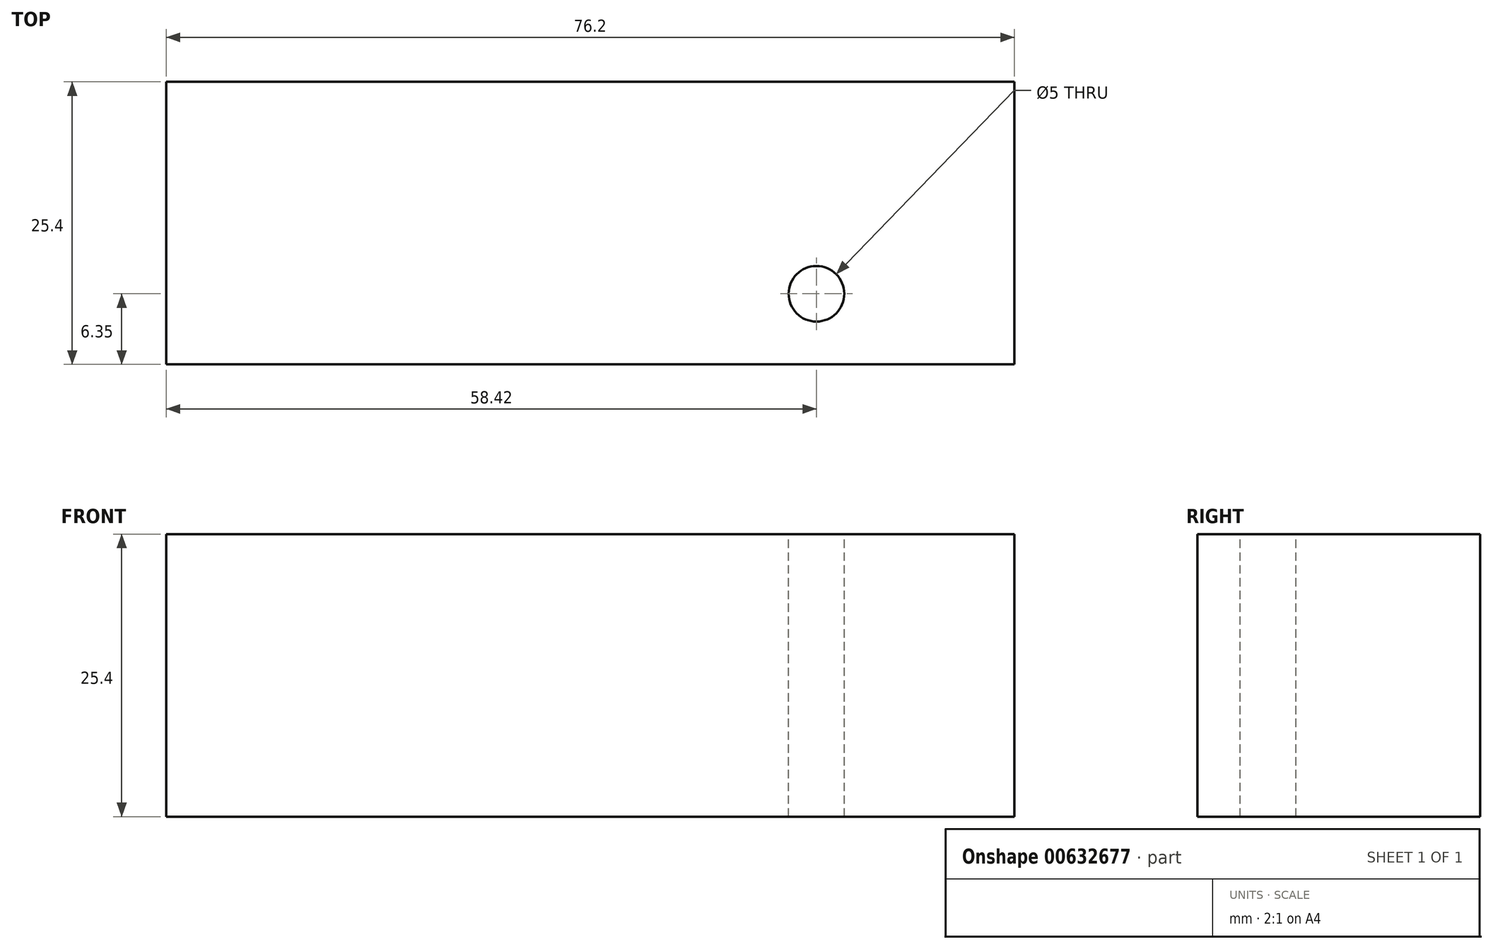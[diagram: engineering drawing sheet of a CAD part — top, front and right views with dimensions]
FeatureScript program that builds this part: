
annotation { "Feature Type Name" : "Feature", "Feature Type Description" : "" }
export const myFeature = defineFeature(function(context is Context, id is Id, definition is map)
    precondition{}
    {
        {
            var Q0;
            Q0=qCreatedBy(makeId("Front.planeOp"),FACE);
            var sketch = newSketch(context, id + "F0", { "sketchPlane" : qUnion([Q0])});
            skLineSegment(sketch, "E0.bottom", {"start": v(38.1, -12.7) * mm, "end": v(-38.1, -12.7) * mm});
            skLineSegment(sketch, "E0.top", {"start": v(38.1, 12.7) * mm, "end": v(-38.1, 12.7) * mm});
            skLineSegment(sketch, "E0.left", {"start": v(38.1, -12.7) * mm, "end": v(38.1, 12.7) * mm});
            skLineSegment(sketch, "E0.right", {"start": v(-38.1, -12.7) * mm, "end": v(-38.1, 12.7) * mm});
            skPoint(sketch, "E0.middle", {"position": v(0, 0) * mm});
            skSolve(sketch);
        }
        {
            var Q0;
            Q0 = qSketchRegion(id + "F0", true);
            extrude(context, id + "F1", {"entities" : qUnion([Q0]), "depth" : 25.4 * mm, "offsetDistance" : 25.4 * mm});
        }
        {
            var Q0;
            Q0=makeQuery(id+"F1.opExtrude","SWEPT_FACE",FACE,{"disambiguationData":[OSD([sQuery(id+"F0.wireOp",EDGE,"E0.top")])]});
            var sketch = newSketch(context, id + "F2", { "sketchPlane" : qUnion([Q0])});
            skPoint(sketch, "E1", {"position": v(20.32, -19.05) * mm});
            skSolve(sketch);
        }
        {
            var Q0;
            Q0=sQuery(id+"F2.wireOp",VERTEX,"E1");
            var Q1;
            Q1=makeQuery(id+"F1.opExtrude","SWEPT_BODY",BODY,{"disambiguationData":[OSD([sQuery(id+"F0.wireOp",EDGE,"E0.bottom"),sQuery(id+"F0.wireOp",EDGE,"E0.top"),sQuery(id+"F0.wireOp",EDGE,"E0.left"),sQuery(id+"F0.wireOp",EDGE,"E0.right")])]});
            hole(context, id + "F3", {"style" : HoleStyle.SIMPLE, "endStyle" : HoleEndStyle.THROUGH, "standardTappedOrClearance" : lookupTablePath({ "standard" : "ISO", "engagement" : "75%", "pitch" : "1 mm", "size" : "M6", "type" : "Tapped" }), "standardBlindInLast" : lookupTablePath({ "standard" : "ISO", "engagement" : "75%", "pitch" : "1 mm", "size" : "M6", "type" : "Tapped" }), "holeDiameter" : 5 * mm, "majorDiameter" : 6 * mm, "showTappedDepth" : true, "isTappedThrough" : true, "tappedDepth" : 12.7 * mm, "tapClearance" : 3, "locations" : qUnion([Q0]), "scope" : qUnion([Q1])});
        }
    });
